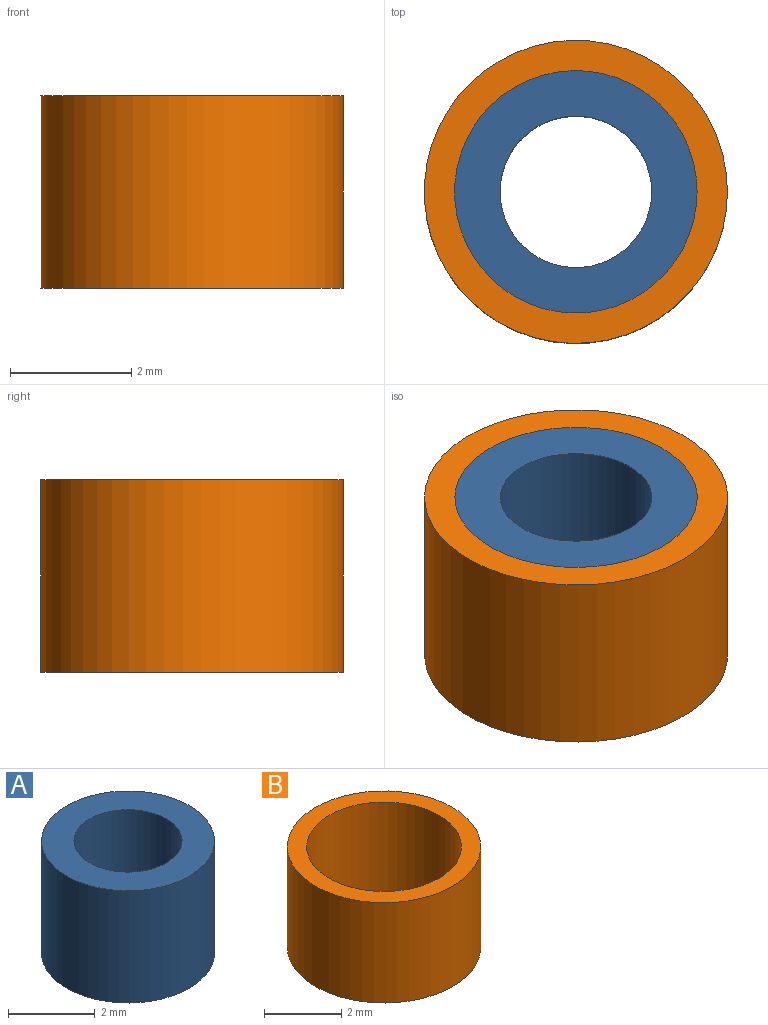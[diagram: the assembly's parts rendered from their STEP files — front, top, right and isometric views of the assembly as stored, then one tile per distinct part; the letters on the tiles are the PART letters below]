
ASSEMBLY  parts=2 mates=1
PART A: 4 faces, bbox 4x4x3.2 mm
  f0: cylinder r=1.25mm len=3.18mm, axis (0,0,-1), area 24.9mm2, adj f2,f3
  f1: cylinder r=2mm len=4mm, axis (0,0,-1), area 39.9mm2, adj f2,f3
  f2: plane 4x4mm, normal (0,0,1), area 7.7mm2, adj f0,f1
  f3: plane 4x4mm, normal (0,0,-1), area 7.7mm2, adj f0,f1
PART B: 4 faces, bbox 5x5x3.2 mm
  f0: cylinder r=2mm len=4mm, axis (0,0,-1), area 39.9mm2, adj f2,f3
  f1: cylinder r=2.5mm len=5mm, axis (0,0,-1), area 49.9mm2, adj f2,f3
  f2: plane 5x5mm, normal (0,0,1), area 7.1mm2, adj f0,f1
  f3: plane 5x5mm, normal (0,0,-1), area 7.1mm2, adj f0,f1
PLACE A at identity
PLACE B at identity
MATE revolute B.f0 <-> A.f0  axis (0,0,1) through (70.23,61.84,4.76)mm
